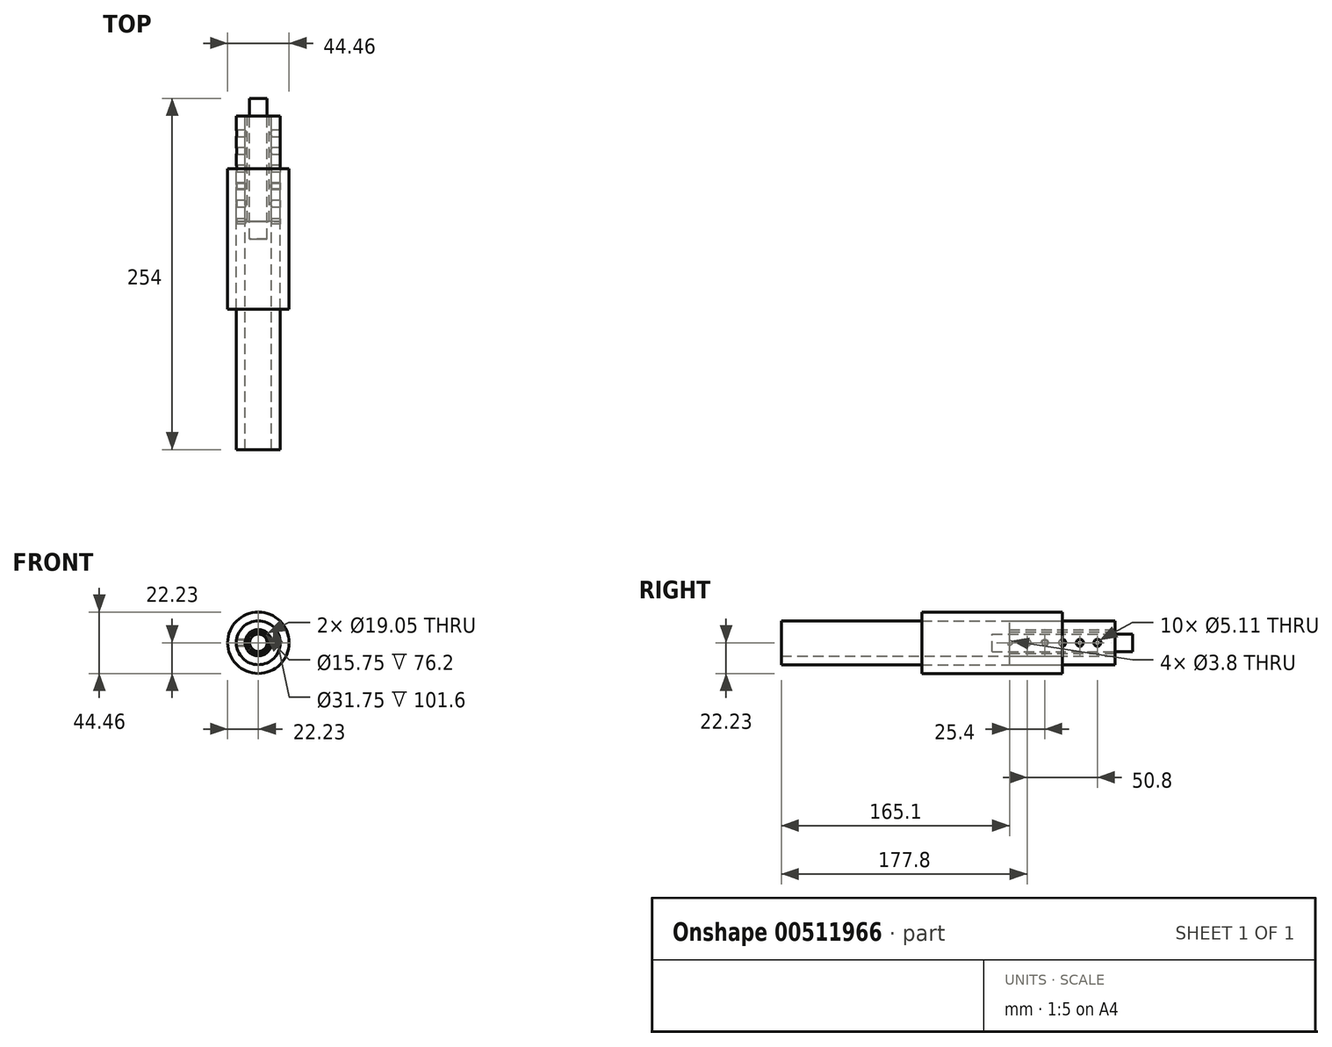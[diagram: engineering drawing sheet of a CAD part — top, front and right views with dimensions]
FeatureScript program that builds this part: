
annotation { "Feature Type Name" : "Feature", "Feature Type Description" : "" }
export const myFeature = defineFeature(function(context is Context, id is Id, definition is map)
    precondition{}
    {
        {
            var Q0;
            Q0=qCreatedBy(makeId("Front.planeOp"),FACE);
            var sketch = newSketch(context, id + "F0", { "sketchPlane" : qUnion([Q0])});
            skCircle(sketch, "E0", {"center": v(0, 0) * mm, "radius": 9.53 * mm});
            skCircle(sketch, "E1", {"center": v(0, 0) * mm, "radius": 15.88 * mm});
            skCircle(sketch, "E2", {"center": v(0, 0) * mm, "radius": 7.87 * mm});
            skCircle(sketch, "E3", {"center": v(0, 0) * mm, "radius": 6.35 * mm});
            skCircle(sketch, "E4", {"center": v(0, 0) * mm, "radius": 22.23 * mm});
            skSolve(sketch);
        }
        {
            var Q0;
            Q0=makeQuery(id+"F0.imprint","IMPRINT",FACE,{"disambiguationData":[TD([[makeQuery(id+"F0.imprint","IMPRINT",EDGE,{"derivedFrom":sQuery(id+"F0.wireOp",EDGE,"E0")}),-1.0]])]});
            extrude(context, id + "F1", {"entities" : qUnion([Q0]), "endBound" : BoundingType.SYMMETRIC, "depth" : 76.2 * mm});
        }
        {
            var Q0;
            Q0=makeQuery(id+"F0.imprint","IMPRINT",FACE,{"disambiguationData":[TD([[makeQuery(id+"F0.imprint","IMPRINT",EDGE,{"derivedFrom":sQuery(id+"F0.wireOp",EDGE,"E0")}),1.0]])]});
            var Q1;
            Q1=makeQuery(id+"F1.opExtrude","CAP_FACE",FACE,{"disambiguationData":[OSD([sQuery(id+"F0.wireOp",EDGE,"E0"),sQuery(id+"F0.wireOp",EDGE,"E1")])],"isStart":false});
            var Q2;
            Q2=makeQuery(id+"F1.opExtrude","CAP_FACE",FACE,{"disambiguationData":[OSD([sQuery(id+"F0.wireOp",EDGE,"E0"),sQuery(id+"F0.wireOp",EDGE,"E1")])],"isStart":true});
            extrude(context, id + "F2", {"entities" : qUnion([Q0]), "endBound" : BoundingType.UP_TO_SURFACE, "endBoundEntityFace" : qUnion([Q1]), "depth" : 76.2 * mm, "hasSecondDirection" : true, "secondDirectionBound" : SecondDirectionBoundingType.UP_TO_SURFACE, "secondDirectionOppositeDirection" : true, "secondDirectionBoundEntityFace" : qUnion([Q2]), "secondDirectionDepth" : 25.4 * mm});
        }
        {
            var Q0;
            Q0=qCreatedBy(makeId("Right.planeOp"),FACE);
            cPlane(context, id + "F3", {"entities" : qUnion([Q0]), "cplaneType" : CPlaneType.OFFSET, "offset" : 50.8 * mm, "oppositeDirection" : true, "width" : 152.4 * mm, "height" : 152.4 * mm});
        }
        {
            var Q0;
            Q0=qCreatedBy(id+"F3.planeOp",FACE);
            var sketch = newSketch(context, id + "F4", { "sketchPlane" : qUnion([Q0])});
            skPoint(sketch, "E5", {"position": v(12.7, 0) * mm});
            skPoint(sketch, "E6", {"position": v(-12.7, 0) * mm});
            skPoint(sketch, "E7", {"position": v(0, 0) * mm});
            skPoint(sketch, "E8", {"position": v(25.4, 0) * mm});
            skPoint(sketch, "E9", {"position": v(-25.4, 0) * mm});
            skPoint(sketch, "E10", {"position": v(-38.1, 0) * mm});
            skSolve(sketch);
        }
        {
            var Q0;
            Q0=sQuery(id+"F4.wireOp",VERTEX,"E5");
            var Q1;
            Q1=sQuery(id+"F4.wireOp",VERTEX,"E6");
            var Q2;
            Q2=sQuery(id+"F4.wireOp",VERTEX,"E8");
            var Q3;
            Q3=sQuery(id+"F4.wireOp",VERTEX,"E7");
            var Q4;
            Q4=sQuery(id+"F4.wireOp",VERTEX,"E9");
            var Q5;
            Q5=makeQuery(id+"F1.opExtrude","SWEPT_BODY",BODY,{"disambiguationData":[OSD([sQuery(id+"F0.wireOp",EDGE,"E0"),sQuery(id+"F0.wireOp",EDGE,"E1")])]});
            hole(context, id + "F5", {"style" : HoleStyle.SIMPLE, "endStyle" : HoleEndStyle.THROUGH, "oppositeDirection" : true, "standardTappedOrClearance" : lookupTablePath({ "standard" : "ANSI", "engagement" : "75%", "pitch" : "20 tpi", "size" : "1/4", "type" : "Tapped" }), "standardBlindInLast" : lookupTablePath({ "standard" : "ANSI", "engagement" : "75%", "pitch" : "20 tpi", "size" : "1/4", "type" : "Tapped" }), "holeDiameter" : 5.1 * mm, "showTappedDepth" : true, "isTappedThrough" : true, "tappedDepth" : 12.7 * mm, "tapClearance" : 3, "locations" : qUnion([Q0, Q1, Q2, Q3, Q4]), "scope" : qUnion([Q5]), "majorDiameter" : 6.35 * mm});
        }
        {
            var Q0;
            Q0=makeQuery(id+"F0.imprint","IMPRINT",FACE,{"disambiguationData":[TD([[makeQuery(id+"F0.imprint","IMPRINT",EDGE,{"derivedFrom":sQuery(id+"F0.wireOp",EDGE,"E3")}),1.0]])]});
            extrude(context, id + "F6", {"entities" : qUnion([Q0]), "endBound" : BoundingType.SYMMETRIC, "depth" : 101.6 * mm});
        }
        {
            var Q0;
            Q0=makeQuery(id+"F0.imprint","IMPRINT",FACE,{"disambiguationData":[TD([[makeQuery(id+"F0.imprint","IMPRINT",EDGE,{"derivedFrom":sQuery(id+"F0.wireOp",EDGE,"E0")}),-1.0]])]});
            extrude(context, id + "F7", {"entities" : qUnion([Q0]), "depth" : 203.2 * mm, "offsetDistance" : 25.4 * mm});
        }
        {
            var Q0;
            Q0=sQuery(id+"F4.wireOp",VERTEX,"E6");
            var Q1;
            Q1=sQuery(id+"F4.wireOp",VERTEX,"E10");
            var Q2;
            Q2=makeQuery(id+"F7.opExtrude","SWEPT_BODY",BODY,{"disambiguationData":[OSD([sQuery(id+"F0.wireOp",EDGE,"E0"),sQuery(id+"F0.wireOp",EDGE,"E1")])]});
            hole(context, id + "F8", {"style" : HoleStyle.SIMPLE, "endStyle" : HoleEndStyle.THROUGH, "oppositeDirection" : true, "standardTappedOrClearance" : lookupTablePath({ "standard" : "ANSI", "engagement" : "75%", "pitch" : "24 tpi", "size" : "#10", "type" : "Tapped" }), "standardBlindInLast" : lookupTablePath({ "standard" : "ANSI", "engagement" : "75%", "pitch" : "24 tpi", "size" : "#10", "type" : "Tapped" }), "holeDiameter" : 3.8 * mm, "showTappedDepth" : true, "isTappedThrough" : true, "tappedDepth" : 12.7 * mm, "tapClearance" : 3, "locations" : qUnion([Q0, Q1]), "scope" : qUnion([Q2]), "majorDiameter" : 4.83 * mm});
        }
        {
            var Q0;
            Q0=makeQuery(id+"F0.imprint","IMPRINT",FACE,{"disambiguationData":[TD([[makeQuery(id+"F0.imprint","IMPRINT",EDGE,{"derivedFrom":sQuery(id+"F0.wireOp",EDGE,"E1")}),-1.0]])]});
            extrude(context, id + "F9", {"entities" : qUnion([Q0]), "depth" : 101.6 * mm, "offsetDistance" : 25.4 * mm});
        }
    });
